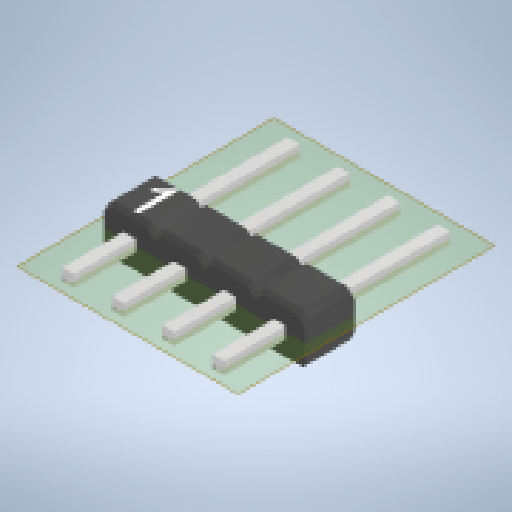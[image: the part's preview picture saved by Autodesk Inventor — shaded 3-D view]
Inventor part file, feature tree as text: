
AUTODESK INVENTOR PART (.ipt)
format: ipt  version: 2023.2 (Build 272271000, 271)  size: 241,664 bytes
history: native  units: in
note: dims shown in document units (in); Inventor stores cm internally (conversion verified against a paired STEP export)
features: plane x2, imported_body x1
ambient origin geometry x8: Origin, YZ Plane, XZ Plane, XY Plane, X Axis, Y Axis, Z Axis, Center Point
bodies: Solid1 (feature_tree)
feature tree (3):
  plane  "Work Plane1"
  plane  "Work Plane2"
  imported_body  "Base1"
